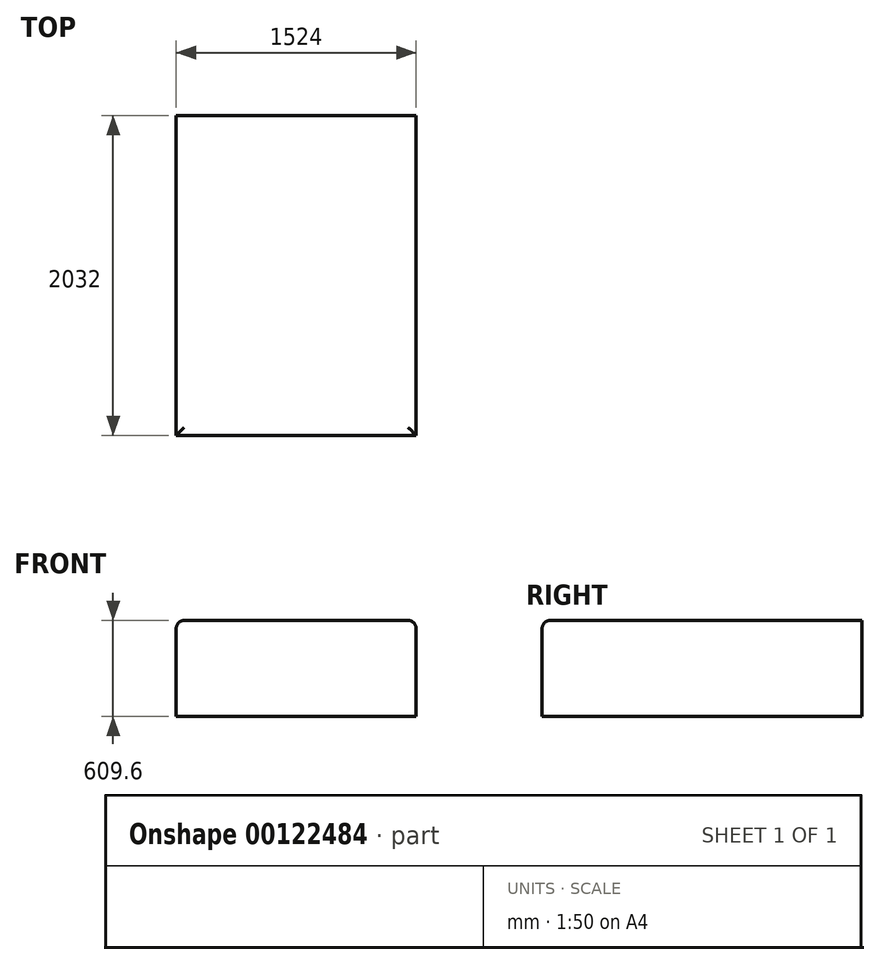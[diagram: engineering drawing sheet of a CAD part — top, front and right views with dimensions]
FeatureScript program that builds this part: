
annotation { "Feature Type Name" : "Feature", "Feature Type Description" : "" }
export const myFeature = defineFeature(function(context is Context, id is Id, definition is map)
    precondition{}
    {
        {
            var Q0;
            Q0=qCreatedBy(makeId("Top.planeOp"),FACE);
            var sketch = newSketch(context, id + "F0", { "sketchPlane" : qUnion([Q0])});
            skLineSegment(sketch, "E0.bottom", {"start": v(0, 0) * mm, "end": v(-1524, 0) * mm});
            skLineSegment(sketch, "E0.top", {"start": v(0, 2032) * mm, "end": v(-1524, 2032) * mm});
            skLineSegment(sketch, "E0.left", {"start": v(0, 0) * mm, "end": v(0, 2032) * mm});
            skLineSegment(sketch, "E0.right", {"start": v(-1524, 0) * mm, "end": v(-1524, 2032) * mm});
            skSolve(sketch);
        }
        {
            var Q0;
            Q0=qSketchRegion(id+"F0",true);
            extrude(context, id + "F1", {"entities" : qUnion([Q0]), "depth" : 609.6 * mm});
        }
        {
            var Q0;
            Q0=makeQuery(id+"F1.opExtrude","CAP_EDGE",EDGE,{"disambiguationData":[OSD([sQuery(id+"F0.wireOp",EDGE,"E0.bottom")])],"isStart":false});
            var Q1;
            Q1=makeQuery(id+"F1.opExtrude","CAP_EDGE",EDGE,{"disambiguationData":[OSD([sQuery(id+"F0.wireOp",EDGE,"E0.right")])],"isStart":false});
            var Q2;
            Q2=makeQuery(id+"F1.opExtrude","CAP_EDGE",EDGE,{"disambiguationData":[OSD([sQuery(id+"F0.wireOp",EDGE,"E0.left")])],"isStart":false});
            fillet(context, id + "F2", {"entities" : qUnion([Q0, Q1, Q2]), "radius" : 50.8 * mm, "tangentPropagation" : true, "allowEdgeOverflow" : false});
        }
    });
